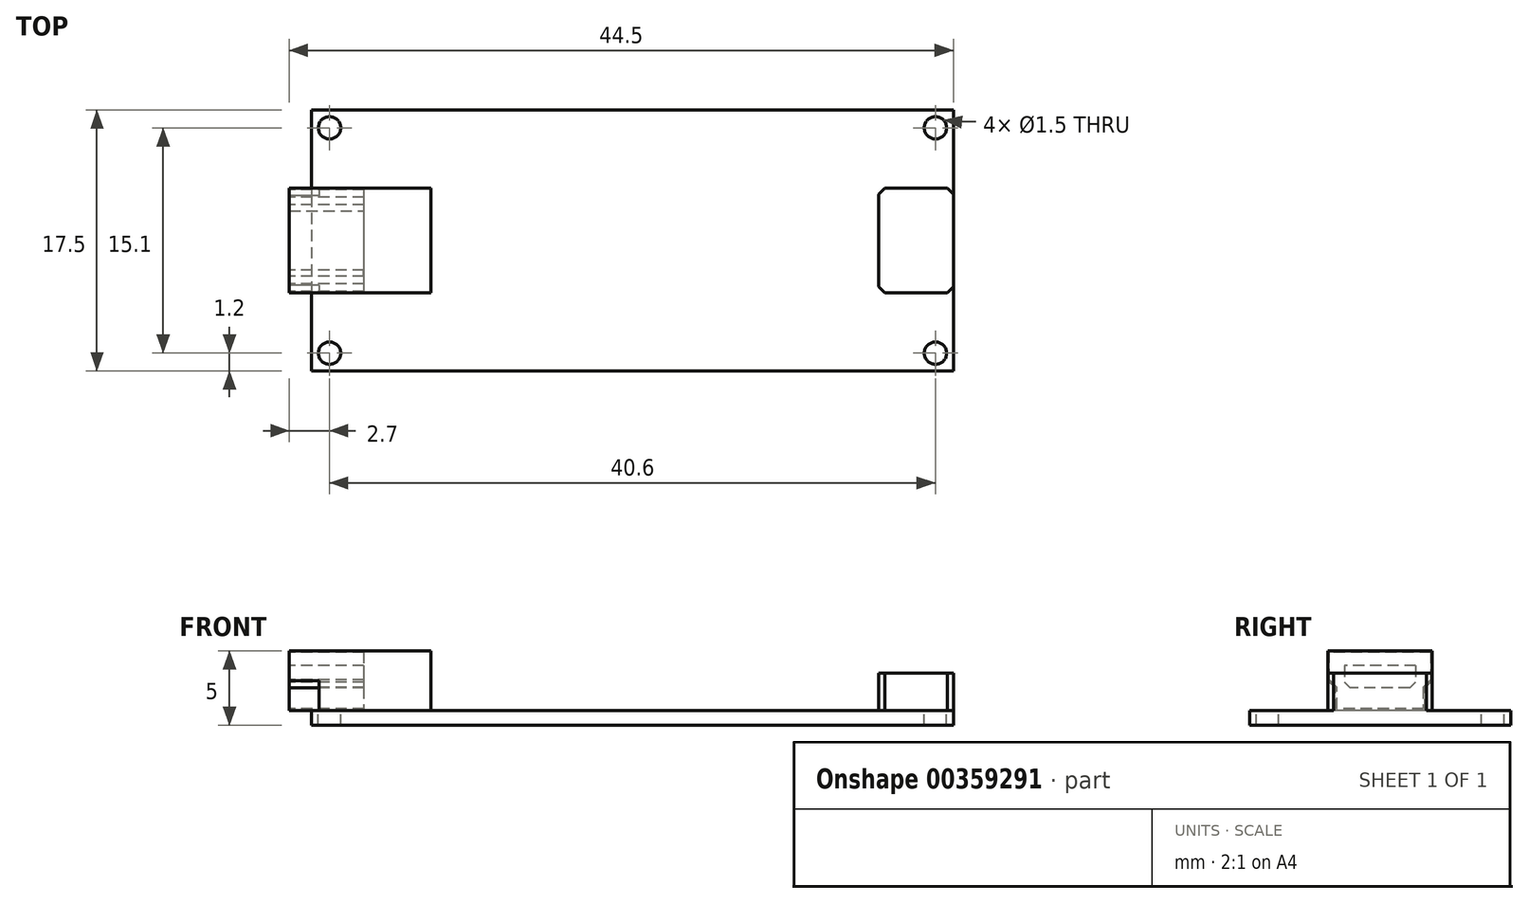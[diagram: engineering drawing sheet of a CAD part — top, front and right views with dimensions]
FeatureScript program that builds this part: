
annotation { "Feature Type Name" : "Feature", "Feature Type Description" : "" }
export const myFeature = defineFeature(function(context is Context, id is Id, definition is map)
    precondition{}
    {
        {
            var Q0;
            Q0=qCreatedBy(makeId("Top.planeOp"),FACE);
            var sketch = newSketch(context, id + "F0", { "sketchPlane" : qUnion([Q0])});
            skLineSegment(sketch, "E0.bottom", {"start": v(21.5, 8.75) * mm, "end": v(-21.5, 8.75) * mm});
            skLineSegment(sketch, "E0.top", {"start": v(21.5, -8.75) * mm, "end": v(-21.5, -8.75) * mm});
            skLineSegment(sketch, "E0.left", {"start": v(21.5, 8.75) * mm, "end": v(21.5, -8.75) * mm});
            skLineSegment(sketch, "E0.right", {"start": v(-21.5, 8.75) * mm, "end": v(-21.5, -8.75) * mm});
            skPoint(sketch, "E0.middle", {"position": v(0, 0) * mm});
            skCircle(sketch, "E1", {"center": v(-20.3, 7.55) * mm, "radius": 0.75 * mm});
            skCircle(sketch, "E2.0.1.0", {"center": v(-20.3, -7.55) * mm, "radius": 0.75 * mm});
            skCircle(sketch, "E2.1.0.0", {"center": v(20.3, 7.55) * mm, "radius": 0.75 * mm});
            skCircle(sketch, "E2.1.1.0", {"center": v(20.3, -7.55) * mm, "radius": 0.75 * mm});
            skLineSegment(sketch, "E2.direction1", {"start": v(-20.3, 7.55) * mm, "end": v(20.3, 7.55) * mm, "construction": true});
            skLineSegment(sketch, "E2.direction2", {"start": v(-20.3, 7.55) * mm, "end": v(-20.3, -7.55) * mm, "construction": true});
            skPoint(sketch, "E3", {"position": v(21.5, 0) * mm});
            skPoint(sketch, "E4", {"position": v(-21.5, 0) * mm});
            skLineSegment(sketch, "E5.bottom", {"start": v(-23, 3.5) * mm, "end": v(-13.5, 3.5) * mm});
            skLineSegment(sketch, "E5.top", {"start": v(-23, -3.5) * mm, "end": v(-13.5, -3.5) * mm});
            skLineSegment(sketch, "E5.left", {"start": v(-23, 3.5) * mm, "end": v(-23, -3.5) * mm});
            skLineSegment(sketch, "E5.right", {"start": v(-13.5, 3.5) * mm, "end": v(-13.5, -3.5) * mm});
            skPoint(sketch, "E6", {"position": v(-13.5, 0) * mm});
            skLineSegment(sketch, "E7.bottom", {"start": v(21.5, 3.5) * mm, "end": v(16.5, 3.5) * mm});
            skLineSegment(sketch, "E7.top", {"start": v(21.5, -3.5) * mm, "end": v(16.5, -3.5) * mm});
            skLineSegment(sketch, "E7.left", {"start": v(21.5, 3.5) * mm, "end": v(21.5, -3.5) * mm});
            skLineSegment(sketch, "E7.right", {"start": v(16.5, 3.5) * mm, "end": v(16.5, -3.5) * mm});
            skSolve(sketch);
        }
        {
            var Q0;
            {var subQ5=sQuery(id+"F0.wireOp",EDGE,"E5.right");Q0=makeQuery(id+"F0.imprint","IMPRINT",FACE,{"disambiguationData":[TD([[makeQuery(id+"F0.imprint","IMPRINT",EDGE,{"derivedFrom":subQ5}),-1.0]])]});}
            var Q1;
            {var subQ0=sQuery(id+"F0.wireOp",EDGE,"E0.bottom");Q1=makeQuery(id+"F0.imprint","IMPRINT",FACE,{"disambiguationData":[TD([[makeQuery(id+"F0.imprint","IMPRINT",EDGE,{"derivedFrom":subQ0}),1.0]])]});}
            var Q2;
            Q2=makeQuery(id+"F0.imprint","IMPRINT",FACE,{"disambiguationData":[TD([[makeQuery(id+"F0.imprint","IMPRINT",EDGE,{"derivedFrom":sQuery(id+"F0.wireOp",EDGE,"E7.bottom")}),1.0]])]});
            extrude(context, id + "F1", {"entities" : qUnion([Q0, Q1, Q2]), "oppositeDirection" : true, "depth" : 1 * mm});
        }
        {
            var Q0;
            {var subQ5=sQuery(id+"F0.wireOp",EDGE,"E5.left");Q0=makeQuery(id+"F0.imprint","IMPRINT",FACE,{"disambiguationData":[TD([[makeQuery(id+"F0.imprint","IMPRINT",EDGE,{"derivedFrom":subQ5}),1.0]])]});}
            var Q1;
            {var subQ5=sQuery(id+"F0.wireOp",EDGE,"E5.right");Q1=makeQuery(id+"F0.imprint","IMPRINT",FACE,{"disambiguationData":[TD([[makeQuery(id+"F0.imprint","IMPRINT",EDGE,{"derivedFrom":subQ5}),-1.0]])]});}
            extrude(context, id + "F2", {"entities" : qUnion([Q0, Q1]), "operationType" : NewBodyOperationType.ADD, "depth" : 4 * mm});
        }
        {
            var Q0;
            Q0=makeQuery(id+"F0.imprint","IMPRINT",FACE,{"disambiguationData":[TD([[makeQuery(id+"F0.imprint","IMPRINT",EDGE,{"derivedFrom":sQuery(id+"F0.wireOp",EDGE,"E7.bottom")}),1.0]])]});
            extrude(context, id + "F3", {"entities" : qUnion([Q0]), "operationType" : NewBodyOperationType.ADD, "depth" : 2.5 * mm});
        }
        {
            var Q0;
            Q0=makeQuery(id+"F2.opExtrude","SWEPT_FACE",FACE,{"disambiguationData":[OSD([sQuery(id+"F0.wireOp",EDGE,"E5.left")])]});
            var sketch = newSketch(context, id + "F4", { "sketchPlane" : qUnion([Q0])});
            skPoint(sketch, "E8", {"position": v(-3.5, 2) * mm});
            skPoint(sketch, "E9", {"position": v(3.5, 2) * mm});
            skPoint(sketch, "E10", {"position": v(-3, 0) * mm});
            skPoint(sketch, "E11", {"position": v(3, 0) * mm});
            skPoint(sketch, "E12", {"position": v(-3, 1.5) * mm});
            skPoint(sketch, "E13", {"position": v(3, 1.5) * mm});
            skLineSegment(sketch, "E14", {"start": v(-3.5, 2) * mm, "end": v(-3, 1.5) * mm});
            skLineSegment(sketch, "E15", {"start": v(-3, 0) * mm, "end": v(-3, 1.5) * mm});
            skLineSegment(sketch, "E16", {"start": v(3, 0) * mm, "end": v(3, 1.5) * mm});
            skLineSegment(sketch, "E17", {"start": v(3, 1.5) * mm, "end": v(3.5, 2) * mm});
            skLineSegment(sketch, "E18.bottom", {"start": v(-2.4, 3) * mm, "end": v(2.4, 3) * mm});
            skLineSegment(sketch, "E18.top", {"start": v(-2.4, 1.5) * mm, "end": v(2.4, 1.5) * mm});
            skLineSegment(sketch, "E18.left", {"start": v(-2.4, 3) * mm, "end": v(-2.4, 1.5) * mm});
            skLineSegment(sketch, "E18.right", {"start": v(2.4, 3) * mm, "end": v(2.4, 1.5) * mm});
            skPoint(sketch, "E19", {"position": v(0, 3) * mm});
            skPoint(sketch, "E20", {"position": v(-2.4, 2.25) * mm});
            skPoint(sketch, "E21", {"position": v(-3.5, 4) * mm});
            skPoint(sketch, "E22", {"position": v(3.5, 4) * mm});
            skLineSegment(sketch, "E23.0", {"start": v(-3.5, -1) * mm, "end": v(3.5, -1) * mm});
            skLineSegment(sketch, "E24", {"start": v(-3.5, 4) * mm, "end": v(-3.5, 2) * mm});
            skLineSegment(sketch, "E25", {"start": v(-3, 1.5) * mm, "end": v(-3, 0) * mm});
            skLineSegment(sketch, "E26", {"start": v(-3, 0) * mm, "end": v(3, 0) * mm});
            skLineSegment(sketch, "E27", {"start": v(3.5, 2) * mm, "end": v(3.5, 4) * mm});
            skLineSegment(sketch, "E28.0", {"start": v(-3.4, 3.9) * mm, "end": v(3.4, 3.9) * mm});
            skLineSegment(sketch, "E28.1", {"start": v(3.4, 2.04) * mm, "end": v(3.4, 3.9) * mm});
            skLineSegment(sketch, "E28.2", {"start": v(-3.4, 3.9) * mm, "end": v(-3.4, 2.04) * mm});
            skLineSegment(sketch, "E28.3", {"start": v(2.9, 1.54) * mm, "end": v(3.4, 2.04) * mm});
            skLineSegment(sketch, "E28.4", {"start": v(-3.4, 2.04) * mm, "end": v(-2.9, 1.54) * mm});
            skLineSegment(sketch, "E28.5", {"start": v(-2.9, 1.54) * mm, "end": v(-2.9, 0.1) * mm});
            skLineSegment(sketch, "E28.6", {"start": v(-2.9, 0.1) * mm, "end": v(2.9, 0.1) * mm});
            skLineSegment(sketch, "E28.7", {"start": v(2.9, 0.1) * mm, "end": v(2.9, 1.54) * mm});
            skPoint(sketch, "E29", {"position": v(-3.4, 2.04) * mm});
            skPoint(sketch, "E30", {"position": v(-2.9, 1.54) * mm});
            skSolve(sketch);
        }
        {
            var Q0;
            Q0=makeQuery(id+"F4.imprint","IMPRINT",FACE,{"disambiguationData":[TD([[makeQuery(id+"F4.imprint","IMPRINT",EDGE,{"derivedFrom":sQuery(id+"F4.wireOp",EDGE,"E18.bottom")}),1.0]])]});
            extrude(context, id + "F5", {"entities" : qUnion([Q0]), "operationType" : NewBodyOperationType.REMOVE, "oppositeDirection" : true, "depth" : 5 * mm});
        }
        {
            var Q0;
            {var subQ0=sQuery(id+"F4.wireOp",EDGE,"E14");Q0=makeQuery(id+"F4.imprint","IMPRINT",FACE,{"disambiguationData":[TD([[makeQuery(id+"F4.imprint","IMPRINT",EDGE,{"derivedFrom":subQ0}),-1.0]])]});}
            var Q1;
            {var subQ0=sQuery(id+"F4.wireOp",EDGE,"E16");Q1=makeQuery(id+"F4.imprint","IMPRINT",FACE,{"disambiguationData":[TD([[makeQuery(id+"F4.imprint","IMPRINT",EDGE,{"derivedFrom":subQ0}),-1.0]])]});}
            extrude(context, id + "F6", {"entities" : qUnion([Q0, Q1]), "operationType" : NewBodyOperationType.REMOVE, "oppositeDirection" : true, "depth" : 2 * mm});
        }
        {
            var Q0;
            Q0=makeQuery(id+"F5.boolean.opBoolean","COPY",EDGE,{"derivedFrom":makeQuery(id+"F5.opExtrude","SWEPT_EDGE",EDGE,{"disambiguationData":[OSD([sQuery(id+"F4.wireOp",EDGE,"E18.top"),sQuery(id+"F4.wireOp",EDGE,"E18.right")])]})});
            var Q1;
            Q1=makeQuery(id+"F5.boolean.opBoolean","COPY",EDGE,{"derivedFrom":makeQuery(id+"F5.opExtrude","SWEPT_EDGE",EDGE,{"disambiguationData":[OSD([sQuery(id+"F4.wireOp",EDGE,"E18.top"),sQuery(id+"F4.wireOp",EDGE,"E18.left")])]})});
            chamfer(context, id + "F7", {"entities" : qUnion([Q0, Q1]), "width" : 0.4 * mm, "tangentPropagation" : true});
        }
        {
            var Q0;
            Q0=makeQuery(id+"F3.opExtrude","SWEPT_EDGE",EDGE,{"disambiguationData":[OSD([sQuery(id+"F0.wireOp",EDGE,"E0.left"),sQuery(id+"F0.wireOp",EDGE,"E7.bottom"),sQuery(id+"F0.wireOp",EDGE,"E7.left")])]});
            var Q1;
            Q1=makeQuery(id+"F3.opExtrude","SWEPT_EDGE",EDGE,{"disambiguationData":[OSD([sQuery(id+"F0.wireOp",EDGE,"E7.bottom"),sQuery(id+"F0.wireOp",EDGE,"E7.right")])]});
            var Q2;
            Q2=makeQuery(id+"F3.opExtrude","SWEPT_EDGE",EDGE,{"disambiguationData":[OSD([sQuery(id+"F0.wireOp",EDGE,"E0.left"),sQuery(id+"F0.wireOp",EDGE,"E7.top"),sQuery(id+"F0.wireOp",EDGE,"E7.left")])]});
            var Q3;
            Q3=makeQuery(id+"F3.opExtrude","SWEPT_EDGE",EDGE,{"disambiguationData":[OSD([sQuery(id+"F0.wireOp",EDGE,"E7.top"),sQuery(id+"F0.wireOp",EDGE,"E7.right")])]});
            chamfer(context, id + "F8", {"entities" : qUnion([Q0, Q1, Q2, Q3]), "width" : 0.4 * mm, "tangentPropagation" : true});
        }
    });
